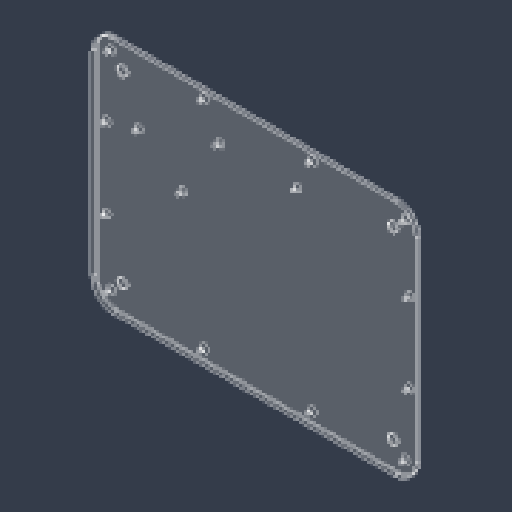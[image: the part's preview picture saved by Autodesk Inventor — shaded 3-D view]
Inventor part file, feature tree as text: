
AUTODESK INVENTOR PART (.ipt)
format: ipt  version: 2023.4 (Build 274418000, 418)  size: 175,616 bytes
history: native  units: mm
features: sketch x5, hole x4, mirror x2, extrude x1, fillet x1, chamfer x1
ambient origin geometry x8: Origin, YZ Plane, XZ Plane, XY Plane, X Axis, Y Axis, Z Axis, Center Point
bodies: Solid1 (feature_tree)
feature tree (14):
  extrude  "Extrusion1"  Depth=220.0mm
  fillet  "Fillet2"  [1 undecoded]
  chamfer  "Chamfer1"  Distance=2.0mm Angle=45.0deg
  hole  "Hole4"  [1 undecoded]
  mirror  "Mirror1"
  mirror  "Mirror2"
  hole  "Hole5"  [1 undecoded]
  hole  "Hole6"  [1 undecoded]
  hole  "Hole7"  [1 undecoded]
  sketch  "Sketch1"  dims[d0=300.0mm d1=220.0mm d3=0.0mm]
  sketch  "Sketch8"  dims[d81=20.0mm d82=1.0mm d83=2.0mm d84=45.0deg]
  sketch  "Sketch9"  dims[d93=3.4mm d94=6.0mm d95=7.5mm d96=3.4mm d97=90.0deg d98=8.0mm d99=20.594885mm d100=14.0mm]
  sketch  "Sketch10"  dims[d101=14.0mm d102=10.0mm]
  sketch  "Sketch11"  dims[d103=10.0mm d104=100.0mm d105=73.0mm d106=25.0mm d107=25.0mm d108=9.0mm d109=6.0mm d110=7.5mm d111=2.0mm d112=90.0deg d113=2.0mm d114=0.0mm d115=71.2mm d116=71.4mm d117=3.4mm d118=6.0mm d119=7.5mm d120=2.9mm d121=90.0deg d122=8.0mm d123=20.594885mm d124=50.5mm d127=3.4mm d128=6.0mm d129=7.5mm d130=2.0mm d131=90.0deg d132=8.0mm d133=20.594885mm d134=15.197537mm d135=88.0mm d136=45.0deg]
note: 5 required parameter values undecoded (feature->parameter linkage not recoverable at this tier; creation-order binding heuristic only, values carry confidence <= 0.55)
